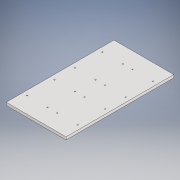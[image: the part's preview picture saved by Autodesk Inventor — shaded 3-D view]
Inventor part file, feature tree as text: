
AUTODESK INVENTOR PART (.ipt)
format: ipt  version: 2019.2 (Build 232265000, 265)  size: 125,952 bytes
history: native  units: mm
features: extrude x2, sketch x2
ambient origin geometry x8: Origin, YZ Plane, XZ Plane, XY Plane, X Axis, Y Axis, Z Axis, Center Point
bodies: Solid1 (feature_tree)
feature tree (4):
  extrude  "Extrusion1"  Depth=175.0mm
  extrude  "Extrusion2"  TaperAngle=0.0deg  [1 undecoded]
  sketch  "Sketch1"  dims[d0=315.0mm d1=175.0mm]
  sketch  "Sketch2"  dims[d2=8.0mm d3=0.0mm d4=20.0mm d6=80.0mm d7=20.0mm d9=60.0mm d12=14.0mm d13=30.0mm d14=3.0mm d15=8.0mm d16=0.0mm]
note: 1 required parameter value undecoded (feature->parameter linkage not recoverable at this tier; creation-order binding heuristic only, values carry confidence <= 0.55)
